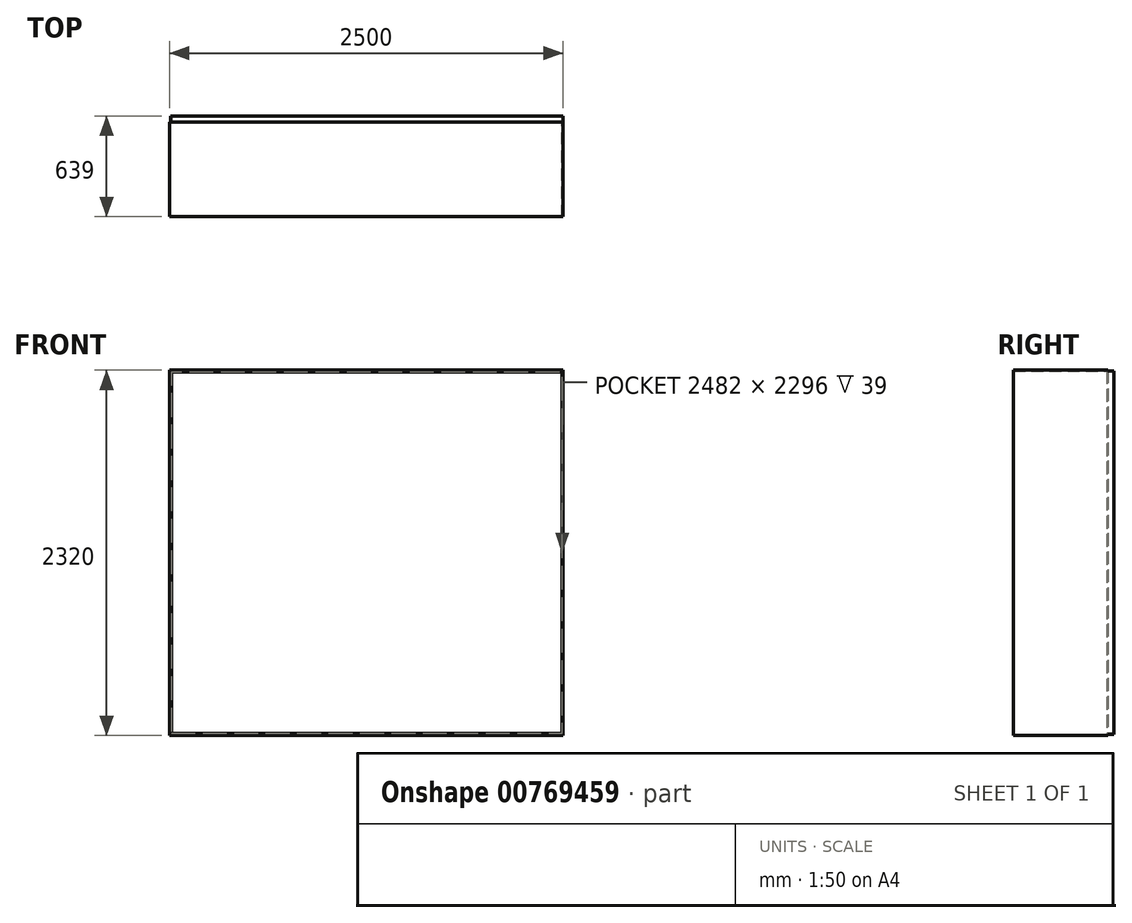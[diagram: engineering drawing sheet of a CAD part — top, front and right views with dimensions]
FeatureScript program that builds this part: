
annotation { "Feature Type Name" : "Feature", "Feature Type Description" : "" }
export const myFeature = defineFeature(function(context is Context, id is Id, definition is map)
    precondition{}
    {
        {
            var Q0;
            Q0=qCreatedBy(makeId("Front.planeOp"),FACE);
            var sketch = newSketch(context, id + "F0", { "sketchPlane" : qUnion([Q0])});
            skLineSegment(sketch, "E0.left", {"start": v(-1250, 677.08) * mm, "end": v(-1250, -677.08) * mm});
            skLineSegment(sketch, "E0.right", {"start": v(1250, 677.08) * mm, "end": v(1250, -677.08) * mm});
            skPoint(sketch, "E0.middle", {"position": v(0, 0) * mm});
            skLineSegment(sketch, "E1.bottom", {"start": v(1250, 1160) * mm, "end": v(-1250, 1160) * mm});
            skLineSegment(sketch, "E1.top", {"start": v(1250, -1160) * mm, "end": v(-1250, -1160) * mm});
            skLineSegment(sketch, "E1.left", {"start": v(1250, 1160) * mm, "end": v(1250, -1160) * mm});
            skLineSegment(sketch, "E1.right", {"start": v(-1250, 1160) * mm, "end": v(-1250, -1160) * mm});
            skSolve(sketch);
        }
        {
            var Q0;
            {var subQ0=sQuery(id+"F0.wireOp",EDGE,"E1.bottom");Q0=makeQuery(id+"F0.imprint","IMPRINT",FACE,{"disambiguationData":[TD([[makeQuery(id+"F0.imprint","IMPRINT",EDGE,{"derivedFrom":subQ0}),1.0]])]});}
            var sketch = newSketch(context, id + "F1", { "sketchPlane" : qUnion([Q0])});
            skLineSegment(sketch, "E2", {"start": v(1246.78, 709.82) * mm, "end": v(-880.19, 709.82) * mm});
            skLineSegment(sketch, "E3", {"start": v(-880.19, 709.82) * mm, "end": v(-880.19, 1166.18) * mm});
            skLineSegment(sketch, "E4", {"start": v(-880.19, -1133.06) * mm, "end": v(-880.19, -730.97) * mm});
            skSolve(sketch);
        }
        {
            var Q0;
            {var subQ0=sQuery(id+"F0.wireOp",EDGE,"E1.bottom");Q0=makeQuery(id+"F0.imprint","IMPRINT",FACE,{"disambiguationData":[TD([[makeQuery(id+"F0.imprint","IMPRINT",EDGE,{"derivedFrom":subQ0}),1.0]])]});}
            extrude(context, id + "F2", {"entities" : qUnion([Q0]), "depth" : 6 * mm, "offsetDistance" : 25 * mm});
        }
        {
            var Q0;
            Q0=makeQuery(id+"F2.opExtrude","CAP_FACE",FACE,{"disambiguationData":[OSD([sQuery(id+"F0.wireOp",EDGE,"E1.bottom"),sQuery(id+"F0.wireOp",EDGE,"E1.top"),sQuery(id+"F0.wireOp",EDGE,"E1.left"),sQuery(id+"F0.wireOp",EDGE,"E1.right")])],"isStart":false});
            var sketch = newSketch(context, id + "F3", { "sketchPlane" : qUnion([Q0])});
            skLineSegment(sketch, "E5.0", {"start": v(-1244, 1160) * mm, "end": v(-1244, -1160) * mm});
            skLineSegment(sketch, "E6.0", {"start": v(1250, 1154) * mm, "end": v(-1250, 1154) * mm});
            skLineSegment(sketch, "E7.0", {"start": v(1256, 1160) * mm, "end": v(1256, -1160) * mm});
            skLineSegment(sketch, "E8.0", {"start": v(1250, -1154) * mm, "end": v(-1250, -1154) * mm});
            skSolve(sketch);
        }
        {
            var Q0;
            Q0 = qSketchRegion(id + "F3", true);
            var Q1;
            {var subQ0=sQuery(id+"F3.wireOp",EDGE,"E6.0");var subQ1=sQuery(id+"F3.wireOp",EDGE,"E5.0");var subQ2=makeQuery(id+"F3.imprint","INTERSECT",VERTEX,{"derivedFrom":[subQ1,subQ0]});Q1=makeQuery(id+"F3.imprint","IMPRINT",FACE,{"disambiguationData":[TD([[makeQuery(id+"F3.imprint","IMPRINT",EDGE,{"disambiguationData":[TD([[subQ2,-1.0]])],"derivedFrom":subQ1}),1.0]])]});}
            extrude(context, id + "F4", {"entities" : qUnion([Q0, Q1]), "operationType" : NewBodyOperationType.ADD, "oppositeDirection" : true, "depth" : 45 * mm, "offsetDistance" : 25 * mm});
        }
        {
            var Q0;
            Q0 = qSketchRegion(id + "F1", true);
            var Q1;
            Q1 = qSketchRegion(id + "F0", true);
            extrude(context, id + "F5", {"entities" : qUnion([Q0, Q1]), "operationType" : NewBodyOperationType.ADD, "depth" : 600 * mm, "offsetDistance" : 25 * mm});
        }
        {
            var Q0;
            Q0=makeQuery(id+"F5.opExtrude","CAP_FACE",FACE,{"disambiguationData":[OSD([sQuery(id+"F0.wireOp",EDGE,"E1.bottom"),sQuery(id+"F0.wireOp",EDGE,"E1.top"),sQuery(id+"F0.wireOp",EDGE,"E1.left"),sQuery(id+"F0.wireOp",EDGE,"E1.right")])],"isStart":false});
            shell(context, id + "F6", {"entities" : qUnion([Q0]), "thickness" : 6 * mm});
        }
    });
